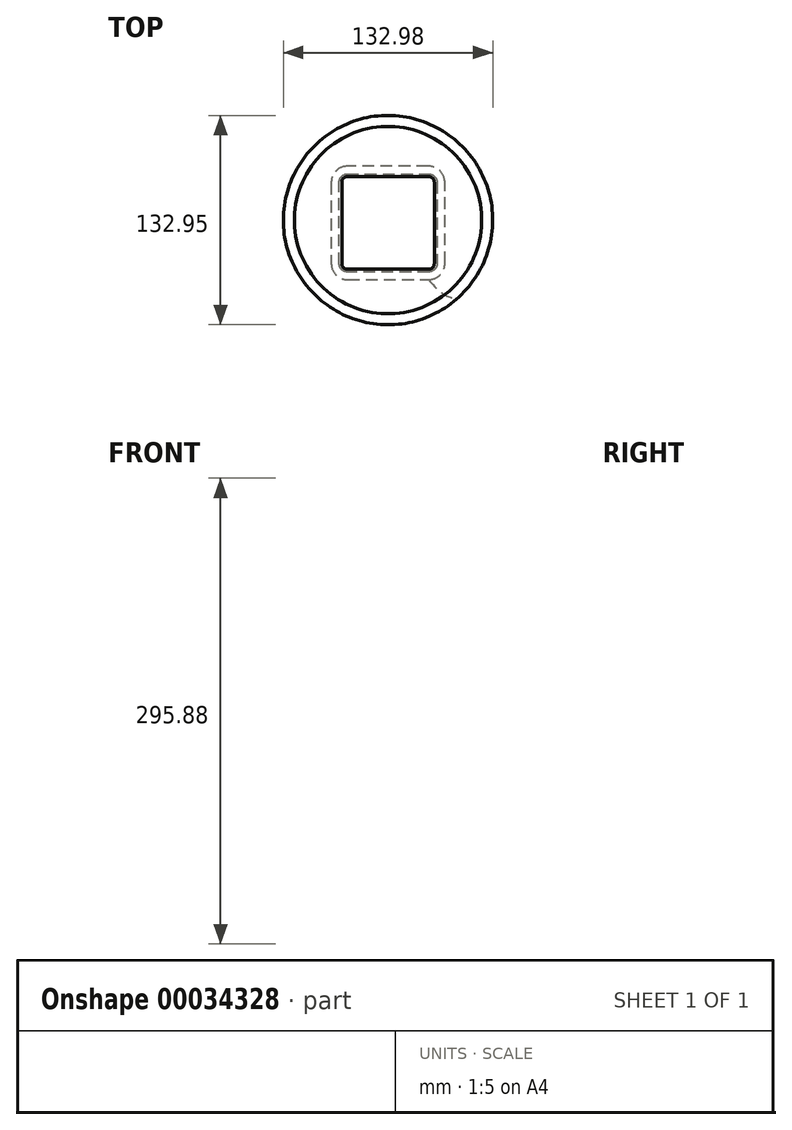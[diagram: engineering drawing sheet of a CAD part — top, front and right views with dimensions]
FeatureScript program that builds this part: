
annotation { "Feature Type Name" : "Feature", "Feature Type Description" : "" }
export const myFeature = defineFeature(function(context is Context, id is Id, definition is map)
    precondition{}
    {
        {
            var Q0;
            Q0=qCreatedBy(makeId("Top.planeOp"),FACE);
            var sketch = newSketch(context, id + "F0", { "sketchPlane" : qUnion([Q0])});
            skLineSegment(sketch, "E0.rect.bottom", {"start": v(25.85, -29.35) * mm, "end": v(-25.85, -29.35) * mm});
            skLineSegment(sketch, "E0.rect.top", {"start": v(25.85, 29.35) * mm, "end": v(-25.85, 29.35) * mm});
            skLineSegment(sketch, "E0.rect.left", {"start": v(29.35, -25.85) * mm, "end": v(29.35, 25.85) * mm});
            skLineSegment(sketch, "E0.rect.right", {"start": v(-29.35, -25.85) * mm, "end": v(-29.35, 25.85) * mm});
            skPoint(sketch, "E0.rect.middle", {"position": v(0, 0) * mm});
            skPoint(sketch, "E1.visualSharp", {"position": v(29.35, 29.35) * mm});
            skArc(sketch, "E1.filletArc", {"start": v(29.35, 25.85) * mm, "mid": v(28.32, 28.32) * mm, "end": v(25.85, 29.35) * mm});
            skPoint(sketch, "E2.visualSharp", {"position": v(-29.35, 29.35) * mm});
            skArc(sketch, "E2.filletArc", {"start": v(-25.85, 29.35) * mm, "mid": v(-28.32, 28.32) * mm, "end": v(-29.35, 25.85) * mm});
            skPoint(sketch, "E3.visualSharp", {"position": v(29.35, -29.35) * mm});
            skArc(sketch, "E3.filletArc", {"start": v(25.85, -29.35) * mm, "mid": v(28.32, -28.32) * mm, "end": v(29.35, -25.85) * mm});
            skPoint(sketch, "E4.visualSharp", {"position": v(-29.35, -29.35) * mm});
            skArc(sketch, "E4.filletArc", {"start": v(-29.35, -25.85) * mm, "mid": v(-28.32, -28.32) * mm, "end": v(-25.85, -29.35) * mm});
            skSolve(sketch);
        }
        {
            var Q0;
            Q0=qCreatedBy(makeId("Top.planeOp"),FACE);
            cPlane(context, id + "F1", {"entities" : qUnion([Q0]), "cplaneType" : CPlaneType.OFFSET, "offset" : 100 * mm, "width" : 150 * mm, "height" : 150 * mm});
        }
        {
            var Q0;
            Q0=qCreatedBy(id+"F1.planeOp",FACE);
            var sketch = newSketch(context, id + "F2", { "sketchPlane" : qUnion([Q0])});
            skLineSegment(sketch, "E5.rect.bottom", {"start": v(33.65, -37.14) * mm, "end": v(-33.65, -37.15) * mm});
            skLineSegment(sketch, "E5.rect.top", {"start": v(33.65, 37.15) * mm, "end": v(-33.65, 37.15) * mm});
            skLineSegment(sketch, "E5.rect.left", {"start": v(37.15, -33.64) * mm, "end": v(37.15, 33.65) * mm});
            skLineSegment(sketch, "E5.rect.right", {"start": v(-37.15, -33.65) * mm, "end": v(-37.15, 33.64) * mm});
            skPoint(sketch, "E5.rect.middle", {"position": v(0, 0) * mm});
            skPoint(sketch, "E6.visualSharp", {"position": v(-37.15, 37.15) * mm});
            skArc(sketch, "E6.filletArc", {"start": v(-33.65, 37.14) * mm, "mid": v(-36.12, 36.12) * mm, "end": v(-37.15, 33.64) * mm});
            skPoint(sketch, "E7.visualSharp", {"position": v(-37.15, -37.15) * mm});
            skArc(sketch, "E7.filletArc", {"start": v(-37.15, -33.65) * mm, "mid": v(-36.12, -36.12) * mm, "end": v(-33.65, -37.15) * mm});
            skPoint(sketch, "E8.visualSharp", {"position": v(37.15, -37.14) * mm});
            skArc(sketch, "E8.filletArc", {"start": v(33.65, -37.14) * mm, "mid": v(36.12, -36.12) * mm, "end": v(37.15, -33.64) * mm});
            skPoint(sketch, "E9.visualSharp", {"position": v(37.15, 37.15) * mm});
            skArc(sketch, "E9.filletArc", {"start": v(37.15, 33.65) * mm, "mid": v(36.12, 36.12) * mm, "end": v(33.65, 37.15) * mm});
            skSolve(sketch);
        }
        {
            var Q0;
            Q0=qCreatedBy(id+"F1.planeOp",FACE);
            cPlane(context, id + "F3", {"entities" : qUnion([Q0]), "cplaneType" : CPlaneType.OFFSET, "offset" : 88.98 * mm, "width" : 150 * mm, "height" : 150 * mm});
        }
        {
            var Q0;
            Q0=qCreatedBy(id+"F3.planeOp",FACE);
            cPlane(context, id + "F4", {"entities" : qUnion([Q0]), "cplaneType" : CPlaneType.OFFSET, "offset" : 100 * mm, "width" : 150 * mm, "height" : 150 * mm});
        }
        {
            var Q0;
            Q0=qCreatedBy(id+"F4.planeOp",FACE);
            var sketch = newSketch(context, id + "F5", { "sketchPlane" : qUnion([Q0])});
            skCircle(sketch, "E10", {"center": v(0, 1.78) * mm, "radius": 59.51 * mm});
            skSolve(sketch);
        }
        {
            var Q0;
            Q0=makeQuery(id+"F0.imprint","IMPRINT",FACE,{"disambiguationData":[TD([[makeQuery(id+"F0.imprint","IMPRINT",EDGE,{"derivedFrom":sQuery(id+"F0.wireOp",EDGE,"E0.rect.bottom")}),-1.0]])]});
            var Q1;
            Q1=makeQuery(id+"F2.imprint","IMPRINT",FACE,{"disambiguationData":[TD([[makeQuery(id+"F2.imprint","IMPRINT",EDGE,{"derivedFrom":sQuery(id+"F2.wireOp",EDGE,"E5.rect.bottom")}),-1.0]])]});
            var Q2;
            Q2=makeQuery(id+"F5.imprint","IMPRINT",FACE,{"disambiguationData":[TD([[makeQuery(id+"F5.imprint","IMPRINT",EDGE,{"derivedFrom":sQuery(id+"F5.wireOp",EDGE,"E10")}),1.0]])]});
            loft(context, id + "F6", {"sheetProfilesArray" : [{ "sheetProfileEntities" : qUnion([Q0]) }, { "sheetProfileEntities" : qUnion([Q1]) }, { "sheetProfileEntities" : qUnion([Q2]) }]});
        }
        {
            var Q0;
            Q0=makeQuery(id+"F6.opLoft","CAP_FACE",FACE,{"disambiguationData":[OSD([makeQuery(id+"F5.imprint","IMPRINT",FACE,{"disambiguationData":[TD([[makeQuery(id+"F5.imprint","IMPRINT",EDGE,{"derivedFrom":sQuery(id+"F5.wireOp",EDGE,"E10")}),1.0]])]})])],"isStart":true});
            var Q1;
            Q1=makeQuery(id+"F6.opLoft","SWEPT_BODY",BODY,{"disambiguationData":[OSD([makeQuery(id+"F0.imprint","IMPRINT",FACE,{"disambiguationData":[TD([[makeQuery(id+"F0.imprint","IMPRINT",EDGE,{"derivedFrom":sQuery(id+"F0.wireOp",EDGE,"E0.rect.bottom")}),-1.0]])]}),sQuery(id+"F2.wireOp",EDGE,"E8.filletArc"),makeQuery(id+"F5.imprint","IMPRINT",FACE,{"disambiguationData":[TD([[makeQuery(id+"F5.imprint","IMPRINT",EDGE,{"derivedFrom":sQuery(id+"F5.wireOp",EDGE,"E10")}),1.0]])]})])]});
            shell(context, id + "F7", {"entities" : qUnion([Q0]), "parts" : qUnion([Q1]), "thickness" : 6.9 * mm, "oppositeDirection" : true});
        }
        {
            var Q0;
            Q0=makeQuery(id+"F6.opLoft","MID_CAP_EDGE",EDGE,{"disambiguationData":[OSD([sQuery(id+"F0.wireOp",EDGE,"E0.rect.top"),sQuery(id+"F0.wireOp",EDGE,"E2.filletArc"),sQuery(id+"F0.wireOp",EDGE,"E1.filletArc")])],"capPos":0.0});
            var Q1;
            Q1=makeQuery(id+"F6.opLoft","MID_CAP_EDGE",EDGE,{"disambiguationData":[OSD([sQuery(id+"F0.wireOp",EDGE,"E0.rect.right"),sQuery(id+"F0.wireOp",EDGE,"E2.filletArc"),sQuery(id+"F0.wireOp",EDGE,"E4.filletArc")])],"capPos":0.0});
            var Q2;
            Q2=makeQuery(id+"F6.opLoft","MID_CAP_EDGE",EDGE,{"disambiguationData":[OSD([sQuery(id+"F0.wireOp",EDGE,"E0.rect.left"),sQuery(id+"F0.wireOp",EDGE,"E3.filletArc"),sQuery(id+"F0.wireOp",EDGE,"E1.filletArc")])],"capPos":0.0});
            var Q3;
            Q3=makeQuery(id+"F6.opLoft","MID_CAP_EDGE",EDGE,{"disambiguationData":[OSD([sQuery(id+"F0.wireOp",EDGE,"E0.rect.bottom"),sQuery(id+"F0.wireOp",EDGE,"E3.filletArc"),sQuery(id+"F0.wireOp",EDGE,"E4.filletArc")])],"capPos":0.0});
            fillet(context, id + "F8", {"entities" : qUnion([Q0, Q1, Q2, Q3]), "radius" : 5 * mm, "tangentPropagation" : true, "allowEdgeOverflow" : false});
        }
    });
